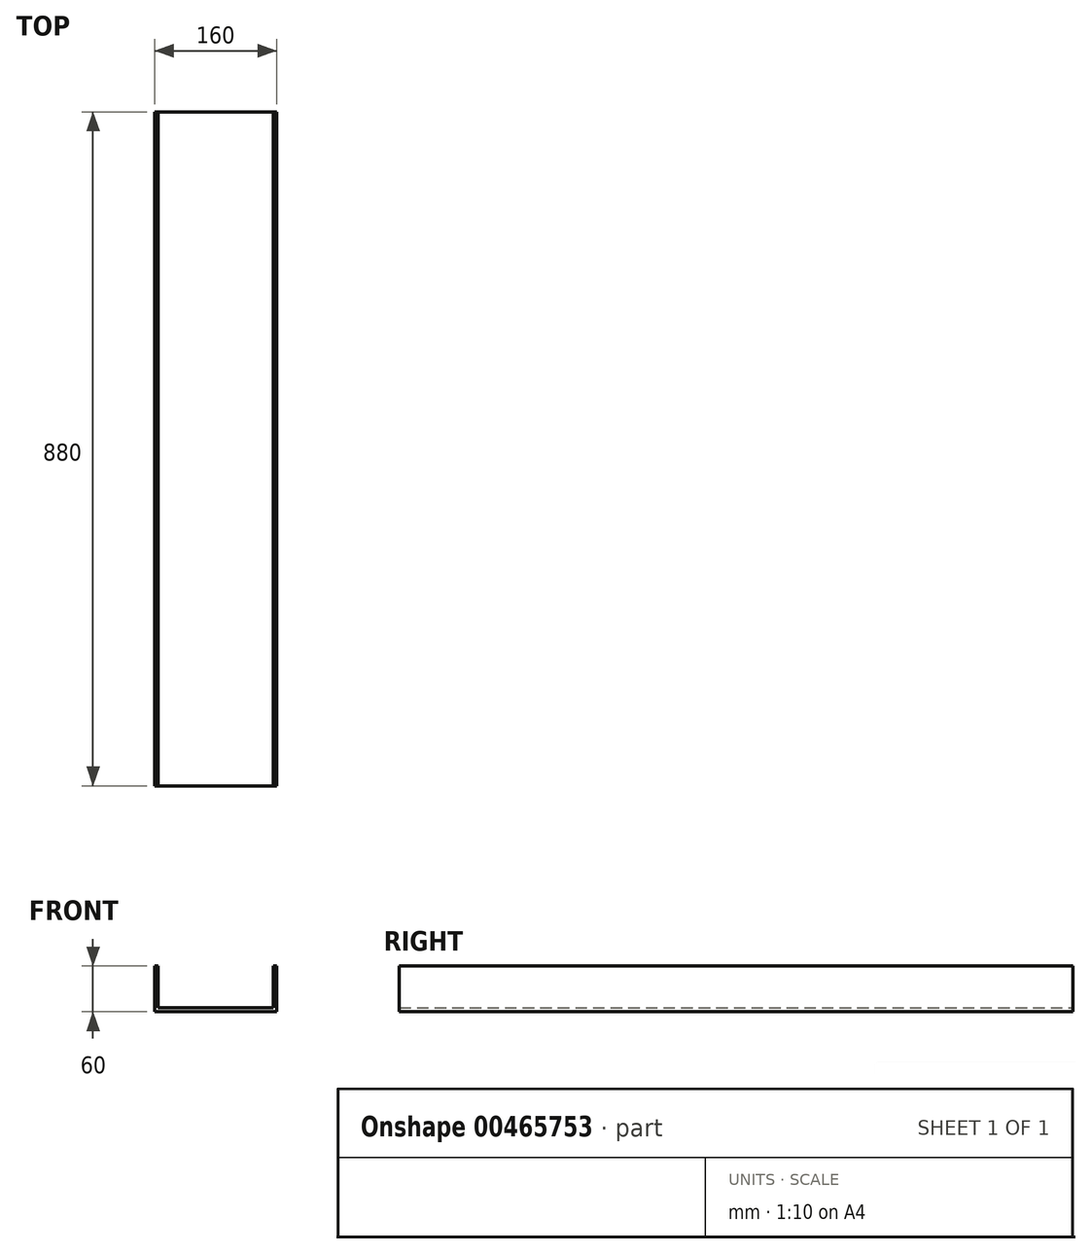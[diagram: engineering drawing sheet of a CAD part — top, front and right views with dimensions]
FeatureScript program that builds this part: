
annotation { "Feature Type Name" : "Feature", "Feature Type Description" : "" }
export const myFeature = defineFeature(function(context is Context, id is Id, definition is map)
    precondition{}
    {
        {
            var Q0;
            Q0=qCreatedBy(makeId("Front.planeOp"),FACE);
            var sketch = newSketch(context, id + "F0", { "sketchPlane" : qUnion([Q0])});
            skLineSegment(sketch, "E0", {"start": v(0, 0) * mm, "end": v(0, 60) * mm});
            skLineSegment(sketch, "E1", {"start": v(0, 0) * mm, "end": v(160, 0) * mm});
            skLineSegment(sketch, "E2", {"start": v(160, 0) * mm, "end": v(160, 60) * mm});
            skLineSegment(sketch, "E3", {"start": v(160, 60) * mm, "end": v(155, 60) * mm});
            skLineSegment(sketch, "E4", {"start": v(155, 60) * mm, "end": v(155, 5) * mm});
            skLineSegment(sketch, "E5", {"start": v(0, 60) * mm, "end": v(5, 60) * mm});
            skLineSegment(sketch, "E6", {"start": v(5, 60) * mm, "end": v(5, 5) * mm});
            skLineSegment(sketch, "E7", {"start": v(5, 5) * mm, "end": v(155, 5) * mm});
            skSolve(sketch);
        }
        {
            var Q0;
            Q0 = qSketchRegion(id + "F0", true);
            extrude(context, id + "F1", {"entities" : qUnion([Q0]), "depth" : 880 * mm, "offsetDistance" : 25 * mm});
        }
    });
